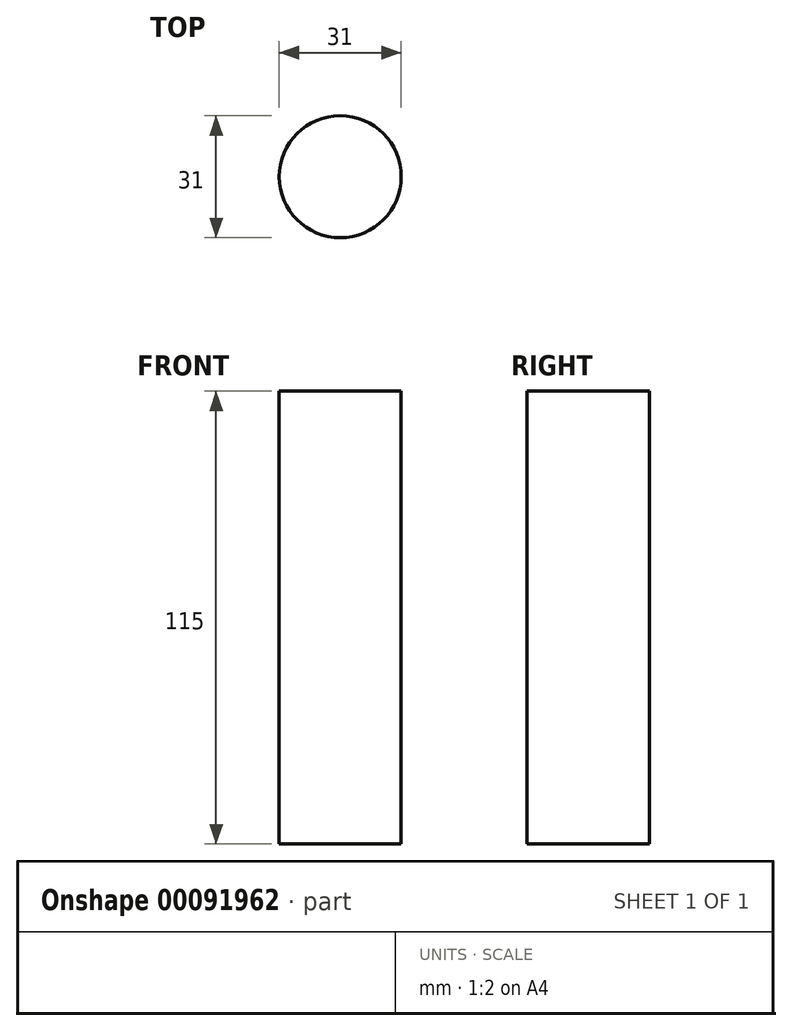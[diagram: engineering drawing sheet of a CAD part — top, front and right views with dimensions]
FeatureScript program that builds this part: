
annotation { "Feature Type Name" : "Feature", "Feature Type Description" : "" }
export const myFeature = defineFeature(function(context is Context, id is Id, definition is map)
    precondition{}
    {
        {
            var Q0;
            Q0=qCreatedBy(makeId("Top.planeOp"),FACE);
            var sketch = newSketch(context, id + "F0", { "sketchPlane" : qUnion([Q0])});
            skCircle(sketch, "E0", {"center": v(0, -1.35) * mm, "radius": 15.5 * mm});
            skSolve(sketch);
        }
        {
            var Q0;
            Q0=makeQuery(id+"F0.imprint","IMPRINT",FACE,{"disambiguationData":[TD([[makeQuery(id+"F0.imprint","IMPRINT",EDGE,{"derivedFrom":sQuery(id+"F0.wireOp",EDGE,"E0")}),1.0]])]});
            extrude(context, id + "F1", {"entities" : qUnion([Q0]), "depth" : 115 * mm});
        }
    });
